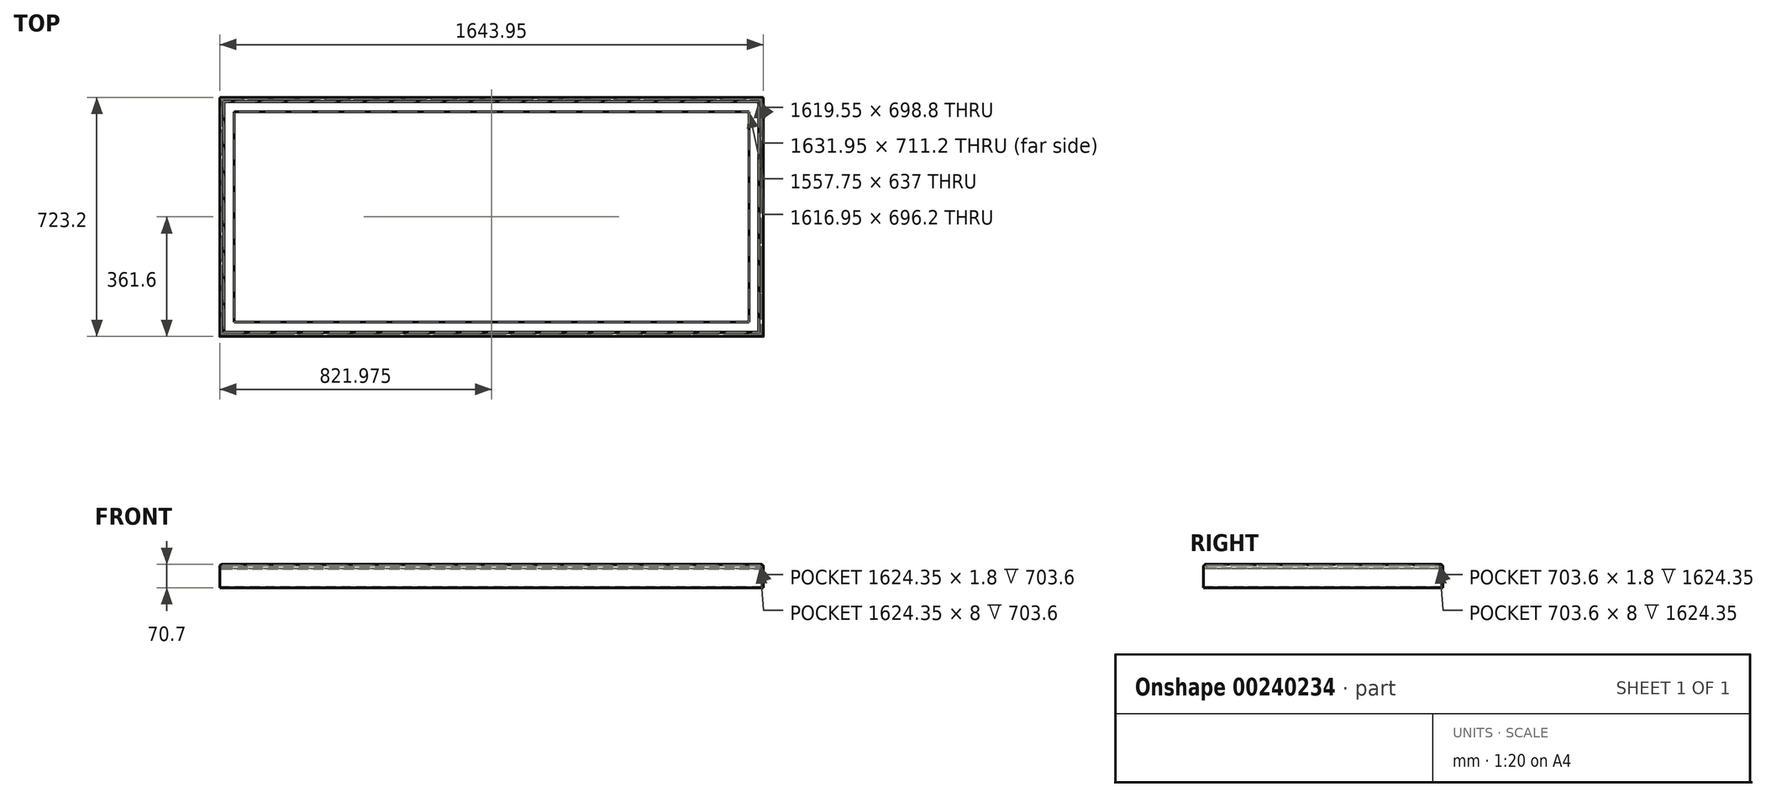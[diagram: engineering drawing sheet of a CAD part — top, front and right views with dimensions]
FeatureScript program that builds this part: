
annotation { "Feature Type Name" : "Feature", "Feature Type Description" : "" }
export const myFeature = defineFeature(function(context is Context, id is Id, definition is map)
    precondition{}
    {
        {
            var Q0;
            Q0=qCreatedBy(makeId("Right.planeOp"),FACE);
            var sketch = newSketch(context, id + "F0", { "sketchPlane" : qUnion([Q0])});
            skLineSegment(sketch, "E0", {"start": v(0, -70.7) * mm, "end": v(0, -6) * mm});
            skLineSegment(sketch, "E1", {"start": v(6, 0) * mm, "end": v(12.2, 0) * mm});
            skLineSegment(sketch, "E2", {"start": v(12.2, 0) * mm, "end": v(12.2, -1.5) * mm});
            skLineSegment(sketch, "E3", {"start": v(12.2, -1.5) * mm, "end": v(9.8, -1.5) * mm});
            skLineSegment(sketch, "E4", {"start": v(9.8, -1.5) * mm, "end": v(9.8, -3.3) * mm});
            skLineSegment(sketch, "E5", {"start": v(9.8, -3.3) * mm, "end": v(13.5, -3.3) * mm});
            skLineSegment(sketch, "E6", {"start": v(13.5, -3.3) * mm, "end": v(13.5, -4.5) * mm});
            skLineSegment(sketch, "E7", {"start": v(13.5, -4.5) * mm, "end": v(9.8, -4.5) * mm});
            skLineSegment(sketch, "E8", {"start": v(9.8, -4.5) * mm, "end": v(9.8, -12.5) * mm});
            skLineSegment(sketch, "E9", {"start": v(9.8, -12.5) * mm, "end": v(43.1, -12.5) * mm});
            skLineSegment(sketch, "E10", {"start": v(43.1, -12.5) * mm, "end": v(43.1, -13.7) * mm});
            skLineSegment(sketch, "E11", {"start": v(43.1, -13.7) * mm, "end": v(8.6, -13.7) * mm});
            skLineSegment(sketch, "E12", {"start": v(8.6, -13.7) * mm, "end": v(8.6, -11.3) * mm});
            skLineSegment(sketch, "E13", {"start": v(8.6, -9.45) * mm, "end": v(8.6, -1.5) * mm});
            skLineSegment(sketch, "E14", {"start": v(8.6, -1.5) * mm, "end": v(6, -1.5) * mm});
            skLineSegment(sketch, "E15", {"start": v(1.5, -6) * mm, "end": v(1.5, -69.5) * mm});
            skLineSegment(sketch, "E16", {"start": v(1.5, -69.5) * mm, "end": v(4.8, -69.5) * mm});
            skLineSegment(sketch, "E17", {"start": v(4.8, -69.5) * mm, "end": v(4.8, -68) * mm});
            skLineSegment(sketch, "E18", {"start": v(4.8, -68) * mm, "end": v(6, -68) * mm});
            skLineSegment(sketch, "E19", {"start": v(6, -68) * mm, "end": v(6, -70.7) * mm});
            skLineSegment(sketch, "E20", {"start": v(6, -70.7) * mm, "end": v(0, -70.7) * mm});
            skLineSegment(sketch, "E21", {"start": v(8.6, -11.3) * mm, "end": v(6.55, -13.7) * mm});
            skLineSegment(sketch, "E22", {"start": v(6.55, -13.7) * mm, "end": v(6, -13.7) * mm});
            skLineSegment(sketch, "E23", {"start": v(6, -13.7) * mm, "end": v(6, -12.5) * mm});
            skLineSegment(sketch, "E24", {"start": v(6, -12.5) * mm, "end": v(8.6, -9.45) * mm});
            skPoint(sketch, "E25.visualSharp", {"position": v(1.5, -1.5) * mm});
            skArc(sketch, "E25.filletArc", {"start": v(6, -1.5) * mm, "mid": v(2.82, -2.82) * mm, "end": v(1.5, -6) * mm});
            skPoint(sketch, "E26.visualSharp", {"position": v(0, 0) * mm});
            skArc(sketch, "E26.filletArc", {"start": v(6, 0) * mm, "mid": v(1.76, -1.76) * mm, "end": v(0, -6) * mm});
            skPoint(sketch, "E27.endSnap0", {"position": v(8.6, -12.5) * mm});
            skSolve(sketch);
        }
        {
            var Q0;
            Q0=qCreatedBy(makeId("Top.planeOp"),FACE);
            var sketch = newSketch(context, id + "F1", { "sketchPlane" : qUnion([Q0])});
            skLineSegment(sketch, "E28.bottom", {"start": v(0, 717.2) * mm, "end": v(1631.95, 717.2) * mm});
            skLineSegment(sketch, "E28.top", {"start": v(0, 6) * mm, "end": v(1631.95, 6) * mm});
            skLineSegment(sketch, "E28.left", {"start": v(0, 717.2) * mm, "end": v(0, 6) * mm});
            skLineSegment(sketch, "E28.right", {"start": v(1631.95, 717.2) * mm, "end": v(1631.95, 6) * mm});
            skSolve(sketch);
        }
        {
            var Q0;
            Q0=makeQuery(id+"F0.imprint","IMPRINT",FACE,{"disambiguationData":[TD([[makeQuery(id+"F0.imprint","IMPRINT",EDGE,{"derivedFrom":sQuery(id+"F0.wireOp",EDGE,"E0")}),-1.0]])]});
            var Q1;
            Q1=sQuery(id+"F1.wireOp",EDGE,"E28.left");
            var Q2;
            Q2=sQuery(id+"F1.wireOp",EDGE,"E28.top");
            var Q3;
            Q3=sQuery(id+"F1.wireOp",EDGE,"E28.right");
            var Q4;
            Q4=sQuery(id+"F1.wireOp",EDGE,"E28.bottom");
            sweep(context, id + "F2", {"profiles" : qUnion([Q0]), "path" : qUnion([Q1, Q2, Q3, Q4])});
        }
    });
